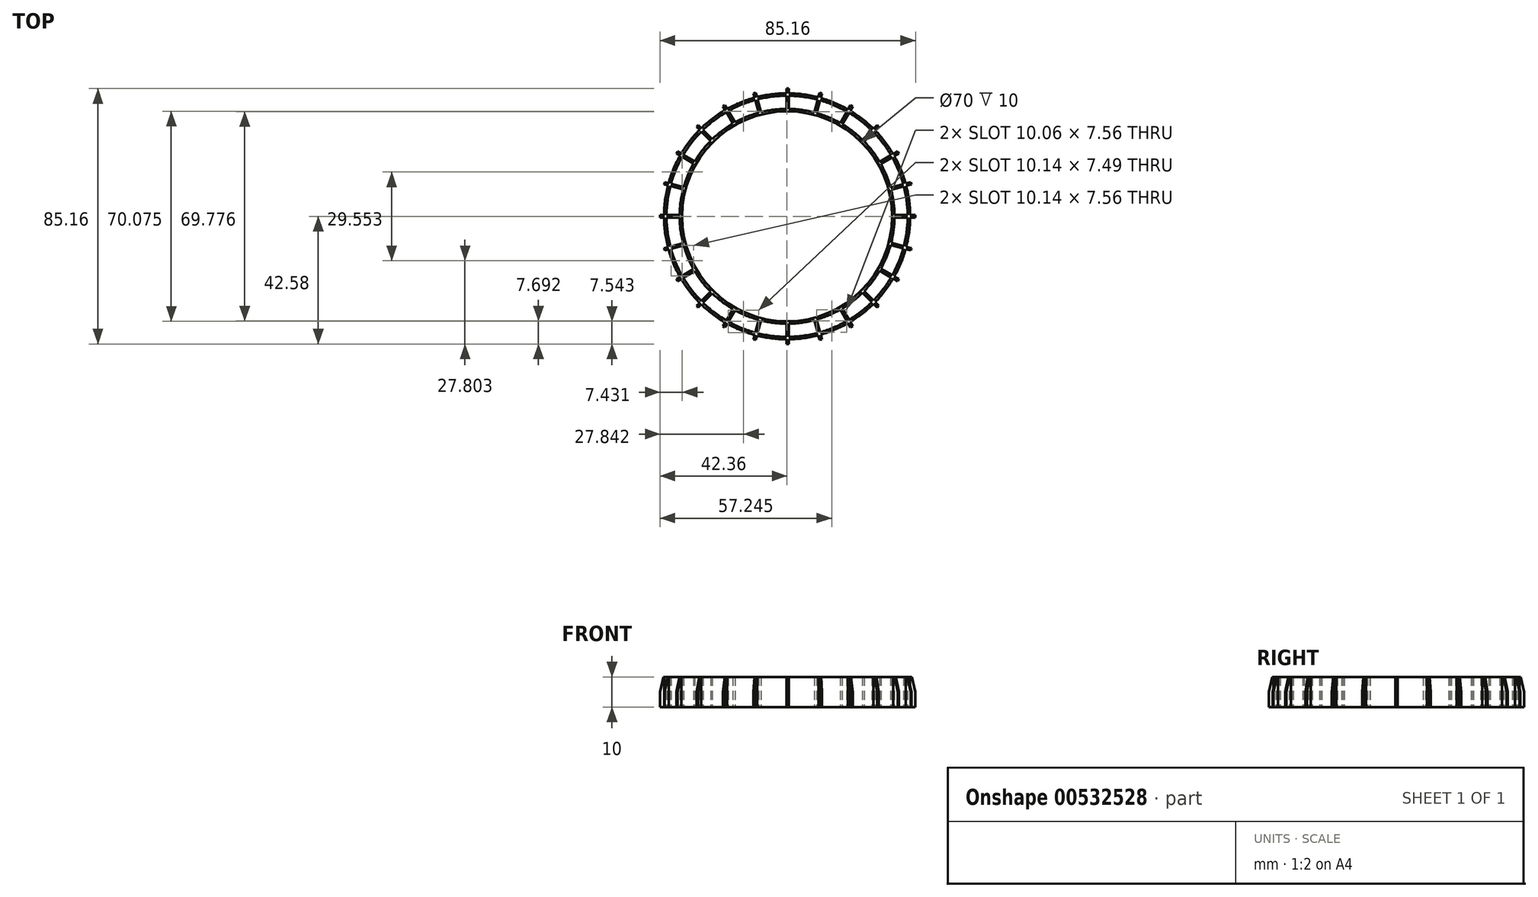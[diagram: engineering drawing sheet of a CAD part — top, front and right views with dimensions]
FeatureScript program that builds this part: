
annotation { "Feature Type Name" : "Feature", "Feature Type Description" : "" }
export const myFeature = defineFeature(function(context is Context, id is Id, definition is map)
    precondition{}
    {
        {
            var Q0;
            Q0=qCreatedBy(makeId("Top.planeOp"),FACE);
            var sketch = newSketch(context, id + "F0", { "sketchPlane" : qUnion([Q0])});
            skCircle(sketch, "E0", {"center": v(0, 0) * mm, "radius": 35 * mm});
            skCircle(sketch, "E1", {"center": v(0, 0) * mm, "radius": 35.8 * mm});
            skCircle(sketch, "E2", {"center": v(0, 0) * mm, "radius": 40.2 * mm});
            skCircle(sketch, "E3", {"center": v(0, 0) * mm, "radius": 41 * mm});
            skLineSegment(sketch, "E4", {"start": v(35.8, 0.4) * mm, "end": v(42.8, 0.4) * mm});
            skLineSegment(sketch, "E5", {"start": v(42.8, 0.4) * mm, "end": v(42.8, 0) * mm});
            skLineSegment(sketch, "E6.MirrorCS", {"start": v(35.8, -0.4) * mm, "end": v(42.8, -0.4) * mm});
            skLineSegment(sketch, "E7.MirrorCS", {"start": v(42.8, -0.4) * mm, "end": v(42.8, 0) * mm});
            skLineSegment(sketch, "E8.1.0", {"start": v(34.48, 9.6) * mm, "end": v(41.24, 11.4) * mm});
            skLineSegment(sketch, "E8.1.1", {"start": v(41.45, 10.63) * mm, "end": v(41.35, 11.02) * mm});
            skLineSegment(sketch, "E8.1.2", {"start": v(41.24, 11.4) * mm, "end": v(41.35, 11.02) * mm});
            skLineSegment(sketch, "E8.1.3", {"start": v(34.69, 8.82) * mm, "end": v(41.45, 10.63) * mm});
            skLineSegment(sketch, "E8.2.0", {"start": v(30.83, 18.14) * mm, "end": v(36.9, 21.64) * mm});
            skLineSegment(sketch, "E8.2.1", {"start": v(37.3, 20.94) * mm, "end": v(37.1, 21.29) * mm});
            skLineSegment(sketch, "E8.2.2", {"start": v(36.9, 21.64) * mm, "end": v(37.1, 21.29) * mm});
            skLineSegment(sketch, "E8.2.3", {"start": v(31.23, 17.44) * mm, "end": v(37.3, 20.94) * mm});
            skLineSegment(sketch, "E8.3.0", {"start": v(25.1, 25.44) * mm, "end": v(30.04, 30.4) * mm});
            skLineSegment(sketch, "E8.3.1", {"start": v(30.6, 29.83) * mm, "end": v(30.33, 30.1) * mm});
            skLineSegment(sketch, "E8.3.2", {"start": v(30.04, 30.4) * mm, "end": v(30.33, 30.1) * mm});
            skLineSegment(sketch, "E8.3.3", {"start": v(25.66, 24.88) * mm, "end": v(30.6, 29.83) * mm});
            skLineSegment(sketch, "E8.4.0", {"start": v(17.66, 31.01) * mm, "end": v(21.16, 37.08) * mm});
            skLineSegment(sketch, "E8.4.1", {"start": v(21.85, 36.68) * mm, "end": v(21.5, 36.88) * mm});
            skLineSegment(sketch, "E8.4.2", {"start": v(21.16, 37.08) * mm, "end": v(21.5, 36.88) * mm});
            skLineSegment(sketch, "E8.4.3", {"start": v(18.35, 30.61) * mm, "end": v(21.85, 36.68) * mm});
            skLineSegment(sketch, "E8.5.0", {"start": v(9.04, 34.47) * mm, "end": v(10.85, 41.23) * mm});
            skLineSegment(sketch, "E8.5.1", {"start": v(11.62, 41.03) * mm, "end": v(11.24, 41.13) * mm});
            skLineSegment(sketch, "E8.5.2", {"start": v(10.85, 41.23) * mm, "end": v(11.24, 41.13) * mm});
            skLineSegment(sketch, "E8.5.3", {"start": v(9.81, 34.26) * mm, "end": v(11.62, 41.03) * mm});
            skLineSegment(sketch, "E8.6.0", {"start": v(-0.18, 35.58) * mm, "end": v(-0.18, 42.58) * mm});
            skLineSegment(sketch, "E8.6.1", {"start": v(0.62, 42.58) * mm, "end": v(0.22, 42.58) * mm});
            skLineSegment(sketch, "E8.6.2", {"start": v(-0.18, 42.58) * mm, "end": v(0.22, 42.58) * mm});
            skLineSegment(sketch, "E8.6.3", {"start": v(0.62, 35.58) * mm, "end": v(0.62, 42.58) * mm});
            skLineSegment(sketch, "E8.7.0", {"start": v(-9.38, 34.26) * mm, "end": v(-11.19, 41.03) * mm});
            skLineSegment(sketch, "E8.7.1", {"start": v(-10.42, 41.23) * mm, "end": v(-10.8, 41.13) * mm});
            skLineSegment(sketch, "E8.7.2", {"start": v(-11.19, 41.03) * mm, "end": v(-10.8, 41.13) * mm});
            skLineSegment(sketch, "E8.7.3", {"start": v(-8.6, 34.47) * mm, "end": v(-10.42, 41.23) * mm});
            skLineSegment(sketch, "E8.8.0", {"start": v(-17.92, 30.61) * mm, "end": v(-21.42, 36.68) * mm});
            skLineSegment(sketch, "E8.8.1", {"start": v(-20.73, 37.08) * mm, "end": v(-21.07, 36.88) * mm});
            skLineSegment(sketch, "E8.8.2", {"start": v(-21.42, 36.68) * mm, "end": v(-21.07, 36.88) * mm});
            skLineSegment(sketch, "E8.8.3", {"start": v(-17.23, 31.01) * mm, "end": v(-20.73, 37.08) * mm});
            skLineSegment(sketch, "E8.9.0", {"start": v(-25.22, 24.88) * mm, "end": v(-30.17, 29.83) * mm});
            skLineSegment(sketch, "E8.9.1", {"start": v(-29.6, 30.4) * mm, "end": v(-29.9, 30.1) * mm});
            skLineSegment(sketch, "E8.9.2", {"start": v(-30.17, 29.83) * mm, "end": v(-29.9, 30.1) * mm});
            skLineSegment(sketch, "E8.9.3", {"start": v(-24.66, 25.44) * mm, "end": v(-29.6, 30.4) * mm});
            skLineSegment(sketch, "E8.10.0", {"start": v(-30.8, 17.44) * mm, "end": v(-36.86, 20.94) * mm});
            skLineSegment(sketch, "E8.10.1", {"start": v(-36.46, 21.64) * mm, "end": v(-36.66, 21.29) * mm});
            skLineSegment(sketch, "E8.10.2", {"start": v(-36.86, 20.94) * mm, "end": v(-36.66, 21.29) * mm});
            skLineSegment(sketch, "E8.10.3", {"start": v(-30.4, 18.14) * mm, "end": v(-36.46, 21.64) * mm});
            skLineSegment(sketch, "E8.11.0", {"start": v(-34.25, 8.82) * mm, "end": v(-41.01, 10.63) * mm});
            skLineSegment(sketch, "E8.11.1", {"start": v(-40.8, 11.4) * mm, "end": v(-40.91, 11.02) * mm});
            skLineSegment(sketch, "E8.11.2", {"start": v(-41.01, 10.63) * mm, "end": v(-40.91, 11.02) * mm});
            skLineSegment(sketch, "E8.11.3", {"start": v(-34.05, 9.6) * mm, "end": v(-40.8, 11.4) * mm});
            skLineSegment(sketch, "E8.12.0", {"start": v(-35.36, -0.4) * mm, "end": v(-42.36, -0.4) * mm});
            skLineSegment(sketch, "E8.12.1", {"start": v(-42.36, 0.4) * mm, "end": v(-42.36, 0) * mm});
            skLineSegment(sketch, "E8.12.2", {"start": v(-42.36, -0.4) * mm, "end": v(-42.36, 0) * mm});
            skLineSegment(sketch, "E8.12.3", {"start": v(-35.36, 0.4) * mm, "end": v(-42.36, 0.4) * mm});
            skLineSegment(sketch, "E8.13.0", {"start": v(-34.05, -9.6) * mm, "end": v(-40.8, -11.4) * mm});
            skLineSegment(sketch, "E8.13.1", {"start": v(-41.01, -10.63) * mm, "end": v(-40.91, -11.02) * mm});
            skLineSegment(sketch, "E8.13.2", {"start": v(-40.8, -11.4) * mm, "end": v(-40.91, -11.02) * mm});
            skLineSegment(sketch, "E8.13.3", {"start": v(-34.25, -8.82) * mm, "end": v(-41.01, -10.63) * mm});
            skLineSegment(sketch, "E8.14.0", {"start": v(-30.4, -18.14) * mm, "end": v(-36.46, -21.64) * mm});
            skLineSegment(sketch, "E8.14.1", {"start": v(-36.86, -20.94) * mm, "end": v(-36.66, -21.29) * mm});
            skLineSegment(sketch, "E8.14.2", {"start": v(-36.46, -21.64) * mm, "end": v(-36.66, -21.29) * mm});
            skLineSegment(sketch, "E8.14.3", {"start": v(-30.8, -17.44) * mm, "end": v(-36.86, -20.94) * mm});
            skLineSegment(sketch, "E8.15.0", {"start": v(-24.66, -25.44) * mm, "end": v(-29.6, -30.4) * mm});
            skLineSegment(sketch, "E8.15.1", {"start": v(-30.17, -29.83) * mm, "end": v(-29.9, -30.1) * mm});
            skLineSegment(sketch, "E8.15.2", {"start": v(-29.6, -30.4) * mm, "end": v(-29.9, -30.1) * mm});
            skLineSegment(sketch, "E8.15.3", {"start": v(-25.22, -24.88) * mm, "end": v(-30.17, -29.83) * mm});
            skLineSegment(sketch, "E8.16.0", {"start": v(-17.23, -31.01) * mm, "end": v(-20.73, -37.08) * mm});
            skLineSegment(sketch, "E8.16.1", {"start": v(-21.42, -36.68) * mm, "end": v(-21.07, -36.88) * mm});
            skLineSegment(sketch, "E8.16.2", {"start": v(-20.73, -37.08) * mm, "end": v(-21.07, -36.88) * mm});
            skLineSegment(sketch, "E8.16.3", {"start": v(-17.92, -30.61) * mm, "end": v(-21.42, -36.68) * mm});
            skLineSegment(sketch, "E8.17.0", {"start": v(-8.6, -34.47) * mm, "end": v(-10.42, -41.23) * mm});
            skLineSegment(sketch, "E8.17.1", {"start": v(-11.19, -41.03) * mm, "end": v(-10.8, -41.13) * mm});
            skLineSegment(sketch, "E8.17.2", {"start": v(-10.42, -41.23) * mm, "end": v(-10.8, -41.13) * mm});
            skLineSegment(sketch, "E8.17.3", {"start": v(-9.38, -34.26) * mm, "end": v(-11.19, -41.03) * mm});
            skLineSegment(sketch, "E8.18.0", {"start": v(0.62, -35.58) * mm, "end": v(0.62, -42.58) * mm});
            skLineSegment(sketch, "E8.18.1", {"start": v(-0.18, -42.58) * mm, "end": v(0.22, -42.58) * mm});
            skLineSegment(sketch, "E8.18.2", {"start": v(0.62, -42.58) * mm, "end": v(0.22, -42.58) * mm});
            skLineSegment(sketch, "E8.18.3", {"start": v(-0.18, -35.58) * mm, "end": v(-0.18, -42.58) * mm});
            skLineSegment(sketch, "E8.19.0", {"start": v(9.81, -34.26) * mm, "end": v(11.62, -41.03) * mm});
            skLineSegment(sketch, "E8.19.1", {"start": v(10.85, -41.23) * mm, "end": v(11.24, -41.13) * mm});
            skLineSegment(sketch, "E8.19.2", {"start": v(11.62, -41.03) * mm, "end": v(11.24, -41.13) * mm});
            skLineSegment(sketch, "E8.19.3", {"start": v(9.04, -34.47) * mm, "end": v(10.85, -41.23) * mm});
            skLineSegment(sketch, "E8.20.0", {"start": v(18.35, -30.61) * mm, "end": v(21.85, -36.68) * mm});
            skLineSegment(sketch, "E8.20.1", {"start": v(21.16, -37.08) * mm, "end": v(21.5, -36.88) * mm});
            skLineSegment(sketch, "E8.20.2", {"start": v(21.85, -36.68) * mm, "end": v(21.5, -36.88) * mm});
            skLineSegment(sketch, "E8.20.3", {"start": v(17.66, -31.01) * mm, "end": v(21.16, -37.08) * mm});
            skLineSegment(sketch, "E8.21.0", {"start": v(25.66, -24.88) * mm, "end": v(30.6, -29.83) * mm});
            skLineSegment(sketch, "E8.21.1", {"start": v(30.04, -30.4) * mm, "end": v(30.33, -30.1) * mm});
            skLineSegment(sketch, "E8.21.2", {"start": v(30.6, -29.83) * mm, "end": v(30.33, -30.1) * mm});
            skLineSegment(sketch, "E8.21.3", {"start": v(25.1, -25.44) * mm, "end": v(30.04, -30.4) * mm});
            skLineSegment(sketch, "E8.22.0", {"start": v(31.23, -17.44) * mm, "end": v(37.3, -20.94) * mm});
            skLineSegment(sketch, "E8.22.1", {"start": v(36.9, -21.64) * mm, "end": v(37.1, -21.29) * mm});
            skLineSegment(sketch, "E8.22.2", {"start": v(37.3, -20.94) * mm, "end": v(37.1, -21.29) * mm});
            skLineSegment(sketch, "E8.22.3", {"start": v(30.83, -18.14) * mm, "end": v(36.9, -21.64) * mm});
            skLineSegment(sketch, "E8.23.0", {"start": v(34.69, -8.82) * mm, "end": v(41.45, -10.63) * mm});
            skLineSegment(sketch, "E8.23.1", {"start": v(41.24, -11.4) * mm, "end": v(41.35, -11.02) * mm});
            skLineSegment(sketch, "E8.23.2", {"start": v(41.45, -10.63) * mm, "end": v(41.35, -11.02) * mm});
            skLineSegment(sketch, "E8.23.3", {"start": v(34.48, -9.6) * mm, "end": v(41.24, -11.4) * mm});
            skPoint(sketch, "E8.center", {"position": v(0.22, 0) * mm});
            skSolve(sketch);
        }
        {
            var Q0;
            {var subQ1=sQuery(id+"F0.wireOp",EDGE,"E8.1.1");Q0=makeQuery(id+"F0.imprint","IMPRINT",FACE,{"disambiguationData":[TD([[makeQuery(id+"F0.imprint","IMPRINT",EDGE,{"derivedFrom":subQ1}),1.0]])]});}
            var Q1;
            {var subQ0=sQuery(id+"F0.wireOp",EDGE,"E8.2.1");Q1=makeQuery(id+"F0.imprint","IMPRINT",FACE,{"disambiguationData":[TD([[makeQuery(id+"F0.imprint","IMPRINT",EDGE,{"derivedFrom":subQ0}),1.0]])]});}
            var Q2;
            {var subQ4=sQuery(id+"F0.wireOp",EDGE,"E8.3.1");Q2=makeQuery(id+"F0.imprint","IMPRINT",FACE,{"disambiguationData":[TD([[makeQuery(id+"F0.imprint","IMPRINT",EDGE,{"derivedFrom":subQ4}),1.0]])]});}
            var Q3;
            {var subQ6=sQuery(id+"F0.wireOp",EDGE,"E8.4.1");Q3=makeQuery(id+"F0.imprint","IMPRINT",FACE,{"disambiguationData":[TD([[makeQuery(id+"F0.imprint","IMPRINT",EDGE,{"derivedFrom":subQ6}),1.0]])]});}
            var Q4;
            {var subQ1=sQuery(id+"F0.wireOp",EDGE,"E8.5.1");Q4=makeQuery(id+"F0.imprint","IMPRINT",FACE,{"disambiguationData":[TD([[makeQuery(id+"F0.imprint","IMPRINT",EDGE,{"derivedFrom":subQ1}),1.0]])]});}
            var Q5;
            {var subQ1=sQuery(id+"F0.wireOp",EDGE,"E8.6.1");Q5=makeQuery(id+"F0.imprint","IMPRINT",FACE,{"disambiguationData":[TD([[makeQuery(id+"F0.imprint","IMPRINT",EDGE,{"derivedFrom":subQ1}),1.0]])]});}
            var Q6;
            {var subQ0=sQuery(id+"F0.wireOp",EDGE,"E8.7.1");Q6=makeQuery(id+"F0.imprint","IMPRINT",FACE,{"disambiguationData":[TD([[makeQuery(id+"F0.imprint","IMPRINT",EDGE,{"derivedFrom":subQ0}),1.0]])]});}
            var Q7;
            {var subQ6=sQuery(id+"F0.wireOp",EDGE,"E8.8.1");Q7=makeQuery(id+"F0.imprint","IMPRINT",FACE,{"disambiguationData":[TD([[makeQuery(id+"F0.imprint","IMPRINT",EDGE,{"derivedFrom":subQ6}),1.0]])]});}
            var Q8;
            {var subQ1=sQuery(id+"F0.wireOp",EDGE,"E8.9.1");Q8=makeQuery(id+"F0.imprint","IMPRINT",FACE,{"disambiguationData":[TD([[makeQuery(id+"F0.imprint","IMPRINT",EDGE,{"derivedFrom":subQ1}),1.0]])]});}
            var Q9;
            {var subQ1=sQuery(id+"F0.wireOp",EDGE,"E8.10.1");Q9=makeQuery(id+"F0.imprint","IMPRINT",FACE,{"disambiguationData":[TD([[makeQuery(id+"F0.imprint","IMPRINT",EDGE,{"derivedFrom":subQ1}),1.0]])]});}
            var Q10;
            {var subQ1=sQuery(id+"F0.wireOp",EDGE,"E8.11.1");Q10=makeQuery(id+"F0.imprint","IMPRINT",FACE,{"disambiguationData":[TD([[makeQuery(id+"F0.imprint","IMPRINT",EDGE,{"derivedFrom":subQ1}),1.0]])]});}
            var Q11;
            {var subQ0=sQuery(id+"F0.wireOp",EDGE,"E8.12.1");Q11=makeQuery(id+"F0.imprint","IMPRINT",FACE,{"disambiguationData":[TD([[makeQuery(id+"F0.imprint","IMPRINT",EDGE,{"derivedFrom":subQ0}),1.0]])]});}
            var Q12;
            {var subQ4=sQuery(id+"F0.wireOp",EDGE,"E8.13.1");Q12=makeQuery(id+"F0.imprint","IMPRINT",FACE,{"disambiguationData":[TD([[makeQuery(id+"F0.imprint","IMPRINT",EDGE,{"derivedFrom":subQ4}),1.0]])]});}
            var Q13;
            {var subQ1=sQuery(id+"F0.wireOp",EDGE,"E8.14.1");Q13=makeQuery(id+"F0.imprint","IMPRINT",FACE,{"disambiguationData":[TD([[makeQuery(id+"F0.imprint","IMPRINT",EDGE,{"derivedFrom":subQ1}),1.0]])]});}
            var Q14;
            {var subQ6=sQuery(id+"F0.wireOp",EDGE,"E8.15.1");Q14=makeQuery(id+"F0.imprint","IMPRINT",FACE,{"disambiguationData":[TD([[makeQuery(id+"F0.imprint","IMPRINT",EDGE,{"derivedFrom":subQ6}),1.0]])]});}
            var Q15;
            {var subQ1=sQuery(id+"F0.wireOp",EDGE,"E8.16.1");Q15=makeQuery(id+"F0.imprint","IMPRINT",FACE,{"disambiguationData":[TD([[makeQuery(id+"F0.imprint","IMPRINT",EDGE,{"derivedFrom":subQ1}),1.0]])]});}
            var Q16;
            {var subQ0=sQuery(id+"F0.wireOp",EDGE,"E8.17.1");Q16=makeQuery(id+"F0.imprint","IMPRINT",FACE,{"disambiguationData":[TD([[makeQuery(id+"F0.imprint","IMPRINT",EDGE,{"derivedFrom":subQ0}),1.0]])]});}
            var Q17;
            {var subQ4=sQuery(id+"F0.wireOp",EDGE,"E8.18.1");Q17=makeQuery(id+"F0.imprint","IMPRINT",FACE,{"disambiguationData":[TD([[makeQuery(id+"F0.imprint","IMPRINT",EDGE,{"derivedFrom":subQ4}),1.0]])]});}
            var Q18;
            {var subQ1=sQuery(id+"F0.wireOp",EDGE,"E8.19.1");Q18=makeQuery(id+"F0.imprint","IMPRINT",FACE,{"disambiguationData":[TD([[makeQuery(id+"F0.imprint","IMPRINT",EDGE,{"derivedFrom":subQ1}),1.0]])]});}
            var Q19;
            {var subQ1=sQuery(id+"F0.wireOp",EDGE,"E8.20.1");Q19=makeQuery(id+"F0.imprint","IMPRINT",FACE,{"disambiguationData":[TD([[makeQuery(id+"F0.imprint","IMPRINT",EDGE,{"derivedFrom":subQ1}),1.0]])]});}
            var Q20;
            {var subQ1=sQuery(id+"F0.wireOp",EDGE,"E8.21.1");Q20=makeQuery(id+"F0.imprint","IMPRINT",FACE,{"disambiguationData":[TD([[makeQuery(id+"F0.imprint","IMPRINT",EDGE,{"derivedFrom":subQ1}),1.0]])]});}
            var Q21;
            {var subQ0=sQuery(id+"F0.wireOp",EDGE,"E8.22.1");Q21=makeQuery(id+"F0.imprint","IMPRINT",FACE,{"disambiguationData":[TD([[makeQuery(id+"F0.imprint","IMPRINT",EDGE,{"derivedFrom":subQ0}),1.0]])]});}
            var Q22;
            {var subQ4=sQuery(id+"F0.wireOp",EDGE,"E8.23.1");Q22=makeQuery(id+"F0.imprint","IMPRINT",FACE,{"disambiguationData":[TD([[makeQuery(id+"F0.imprint","IMPRINT",EDGE,{"derivedFrom":subQ4}),1.0]])]});}
            var Q23;
            {var subQ4=sQuery(id+"F0.wireOp",EDGE,"E5");Q23=makeQuery(id+"F0.imprint","IMPRINT",FACE,{"disambiguationData":[TD([[makeQuery(id+"F0.imprint","IMPRINT",EDGE,{"derivedFrom":subQ4}),-1.0]])]});}
            var Q24;
            {var subQ0=sQuery(id+"F0.wireOp",EDGE,"E8.1.3");var subQ1=sQuery(id+"F0.wireOp",EDGE,"E2");var subQ2=makeQuery(id+"F0.imprint","INTERSECT",VERTEX,{"derivedFrom":[subQ1,subQ0]});Q24=makeQuery(id+"F0.imprint","IMPRINT",FACE,{"disambiguationData":[TD([[makeQuery(id+"F0.imprint","IMPRINT",EDGE,{"disambiguationData":[TD([[subQ2,1.0]])],"derivedFrom":subQ1}),-1.0]])]});}
            var Q25;
            {var subQ0=sQuery(id+"F0.wireOp",EDGE,"E8.1.0");var subQ1=sQuery(id+"F0.wireOp",EDGE,"E2");var subQ2=makeQuery(id+"F0.imprint","INTERSECT",VERTEX,{"derivedFrom":[subQ1,subQ0]});Q25=makeQuery(id+"F0.imprint","IMPRINT",FACE,{"disambiguationData":[TD([[makeQuery(id+"F0.imprint","IMPRINT",EDGE,{"disambiguationData":[TD([[subQ2,-1.0]])],"derivedFrom":subQ1}),-1.0]])]});}
            var Q26;
            {var subQ0=sQuery(id+"F0.wireOp",EDGE,"E8.2.0");var subQ1=sQuery(id+"F0.wireOp",EDGE,"E2");var subQ2=makeQuery(id+"F0.imprint","INTERSECT",VERTEX,{"derivedFrom":[subQ1,subQ0]});Q26=makeQuery(id+"F0.imprint","IMPRINT",FACE,{"disambiguationData":[TD([[makeQuery(id+"F0.imprint","IMPRINT",EDGE,{"disambiguationData":[TD([[subQ2,-1.0]])],"derivedFrom":subQ1}),-1.0]])]});}
            var Q27;
            {var subQ0=sQuery(id+"F0.wireOp",EDGE,"E8.3.0");var subQ1=sQuery(id+"F0.wireOp",EDGE,"E2");var subQ2=makeQuery(id+"F0.imprint","INTERSECT",VERTEX,{"derivedFrom":[subQ1,subQ0]});Q27=makeQuery(id+"F0.imprint","IMPRINT",FACE,{"disambiguationData":[TD([[makeQuery(id+"F0.imprint","IMPRINT",EDGE,{"disambiguationData":[TD([[subQ2,-1.0]])],"derivedFrom":subQ1}),-1.0]])]});}
            var Q28;
            {var subQ0=sQuery(id+"F0.wireOp",EDGE,"E8.4.0");var subQ1=sQuery(id+"F0.wireOp",EDGE,"E2");var subQ2=makeQuery(id+"F0.imprint","INTERSECT",VERTEX,{"derivedFrom":[subQ1,subQ0]});Q28=makeQuery(id+"F0.imprint","IMPRINT",FACE,{"disambiguationData":[TD([[makeQuery(id+"F0.imprint","IMPRINT",EDGE,{"disambiguationData":[TD([[subQ2,-1.0]])],"derivedFrom":subQ1}),-1.0]])]});}
            var Q29;
            {var subQ0=sQuery(id+"F0.wireOp",EDGE,"E8.5.0");var subQ1=sQuery(id+"F0.wireOp",EDGE,"E2");var subQ2=makeQuery(id+"F0.imprint","INTERSECT",VERTEX,{"derivedFrom":[subQ1,subQ0]});Q29=makeQuery(id+"F0.imprint","IMPRINT",FACE,{"disambiguationData":[TD([[makeQuery(id+"F0.imprint","IMPRINT",EDGE,{"disambiguationData":[TD([[subQ2,-1.0]])],"derivedFrom":subQ1}),-1.0]])]});}
            var Q30;
            {var subQ0=sQuery(id+"F0.wireOp",EDGE,"E8.6.0");var subQ1=sQuery(id+"F0.wireOp",EDGE,"E2");var subQ2=makeQuery(id+"F0.imprint","INTERSECT",VERTEX,{"derivedFrom":[subQ1,subQ0]});Q30=makeQuery(id+"F0.imprint","IMPRINT",FACE,{"disambiguationData":[TD([[makeQuery(id+"F0.imprint","IMPRINT",EDGE,{"disambiguationData":[TD([[subQ2,-1.0]])],"derivedFrom":subQ1}),-1.0]])]});}
            var Q31;
            {var subQ0=sQuery(id+"F0.wireOp",EDGE,"E8.7.0");var subQ1=sQuery(id+"F0.wireOp",EDGE,"E2");var subQ2=makeQuery(id+"F0.imprint","INTERSECT",VERTEX,{"derivedFrom":[subQ1,subQ0]});Q31=makeQuery(id+"F0.imprint","IMPRINT",FACE,{"disambiguationData":[TD([[makeQuery(id+"F0.imprint","IMPRINT",EDGE,{"disambiguationData":[TD([[subQ2,-1.0]])],"derivedFrom":subQ1}),-1.0]])]});}
            var Q32;
            {var subQ0=sQuery(id+"F0.wireOp",EDGE,"E8.8.0");var subQ1=sQuery(id+"F0.wireOp",EDGE,"E2");var subQ2=makeQuery(id+"F0.imprint","INTERSECT",VERTEX,{"derivedFrom":[subQ1,subQ0]});Q32=makeQuery(id+"F0.imprint","IMPRINT",FACE,{"disambiguationData":[TD([[makeQuery(id+"F0.imprint","IMPRINT",EDGE,{"disambiguationData":[TD([[subQ2,-1.0]])],"derivedFrom":subQ1}),-1.0]])]});}
            var Q33;
            {var subQ0=sQuery(id+"F0.wireOp",EDGE,"E8.9.0");var subQ1=sQuery(id+"F0.wireOp",EDGE,"E2");var subQ2=makeQuery(id+"F0.imprint","INTERSECT",VERTEX,{"derivedFrom":[subQ1,subQ0]});Q33=makeQuery(id+"F0.imprint","IMPRINT",FACE,{"disambiguationData":[TD([[makeQuery(id+"F0.imprint","IMPRINT",EDGE,{"disambiguationData":[TD([[subQ2,-1.0]])],"derivedFrom":subQ1}),-1.0]])]});}
            var Q34;
            {var subQ0=sQuery(id+"F0.wireOp",EDGE,"E8.10.0");var subQ1=sQuery(id+"F0.wireOp",EDGE,"E2");var subQ2=makeQuery(id+"F0.imprint","INTERSECT",VERTEX,{"derivedFrom":[subQ1,subQ0]});Q34=makeQuery(id+"F0.imprint","IMPRINT",FACE,{"disambiguationData":[TD([[makeQuery(id+"F0.imprint","IMPRINT",EDGE,{"disambiguationData":[TD([[subQ2,-1.0]])],"derivedFrom":subQ1}),-1.0]])]});}
            var Q35;
            {var subQ0=sQuery(id+"F0.wireOp",EDGE,"E8.11.0");var subQ1=sQuery(id+"F0.wireOp",EDGE,"E2");var subQ2=makeQuery(id+"F0.imprint","INTERSECT",VERTEX,{"derivedFrom":[subQ1,subQ0]});Q35=makeQuery(id+"F0.imprint","IMPRINT",FACE,{"disambiguationData":[TD([[makeQuery(id+"F0.imprint","IMPRINT",EDGE,{"disambiguationData":[TD([[subQ2,-1.0]])],"derivedFrom":subQ1}),-1.0]])]});}
            var Q36;
            {var subQ0=sQuery(id+"F0.wireOp",EDGE,"E8.12.0");var subQ1=sQuery(id+"F0.wireOp",EDGE,"E2");var subQ2=makeQuery(id+"F0.imprint","INTERSECT",VERTEX,{"derivedFrom":[subQ1,subQ0]});Q36=makeQuery(id+"F0.imprint","IMPRINT",FACE,{"disambiguationData":[TD([[makeQuery(id+"F0.imprint","IMPRINT",EDGE,{"disambiguationData":[TD([[subQ2,-1.0]])],"derivedFrom":subQ1}),-1.0]])]});}
            var Q37;
            {var subQ0=sQuery(id+"F0.wireOp",EDGE,"E8.13.0");var subQ1=sQuery(id+"F0.wireOp",EDGE,"E2");var subQ2=makeQuery(id+"F0.imprint","INTERSECT",VERTEX,{"derivedFrom":[subQ1,subQ0]});Q37=makeQuery(id+"F0.imprint","IMPRINT",FACE,{"disambiguationData":[TD([[makeQuery(id+"F0.imprint","IMPRINT",EDGE,{"disambiguationData":[TD([[subQ2,-1.0]])],"derivedFrom":subQ1}),-1.0]])]});}
            var Q38;
            {var subQ0=sQuery(id+"F0.wireOp",EDGE,"E8.14.0");var subQ1=sQuery(id+"F0.wireOp",EDGE,"E2");var subQ2=makeQuery(id+"F0.imprint","INTERSECT",VERTEX,{"derivedFrom":[subQ1,subQ0]});Q38=makeQuery(id+"F0.imprint","IMPRINT",FACE,{"disambiguationData":[TD([[makeQuery(id+"F0.imprint","IMPRINT",EDGE,{"disambiguationData":[TD([[subQ2,-1.0]])],"derivedFrom":subQ1}),-1.0]])]});}
            var Q39;
            {var subQ0=sQuery(id+"F0.wireOp",EDGE,"E8.15.0");var subQ1=sQuery(id+"F0.wireOp",EDGE,"E2");var subQ2=makeQuery(id+"F0.imprint","INTERSECT",VERTEX,{"derivedFrom":[subQ1,subQ0]});Q39=makeQuery(id+"F0.imprint","IMPRINT",FACE,{"disambiguationData":[TD([[makeQuery(id+"F0.imprint","IMPRINT",EDGE,{"disambiguationData":[TD([[subQ2,-1.0]])],"derivedFrom":subQ1}),-1.0]])]});}
            var Q40;
            {var subQ0=sQuery(id+"F0.wireOp",EDGE,"E8.16.0");var subQ1=sQuery(id+"F0.wireOp",EDGE,"E2");var subQ2=makeQuery(id+"F0.imprint","INTERSECT",VERTEX,{"derivedFrom":[subQ1,subQ0]});Q40=makeQuery(id+"F0.imprint","IMPRINT",FACE,{"disambiguationData":[TD([[makeQuery(id+"F0.imprint","IMPRINT",EDGE,{"disambiguationData":[TD([[subQ2,-1.0]])],"derivedFrom":subQ1}),-1.0]])]});}
            var Q41;
            {var subQ0=sQuery(id+"F0.wireOp",EDGE,"E8.17.0");var subQ1=sQuery(id+"F0.wireOp",EDGE,"E2");var subQ2=makeQuery(id+"F0.imprint","INTERSECT",VERTEX,{"derivedFrom":[subQ1,subQ0]});Q41=makeQuery(id+"F0.imprint","IMPRINT",FACE,{"disambiguationData":[TD([[makeQuery(id+"F0.imprint","IMPRINT",EDGE,{"disambiguationData":[TD([[subQ2,-1.0]])],"derivedFrom":subQ1}),-1.0]])]});}
            var Q42;
            {var subQ0=sQuery(id+"F0.wireOp",EDGE,"E8.18.0");var subQ1=sQuery(id+"F0.wireOp",EDGE,"E2");var subQ2=makeQuery(id+"F0.imprint","INTERSECT",VERTEX,{"derivedFrom":[subQ1,subQ0]});Q42=makeQuery(id+"F0.imprint","IMPRINT",FACE,{"disambiguationData":[TD([[makeQuery(id+"F0.imprint","IMPRINT",EDGE,{"disambiguationData":[TD([[subQ2,-1.0]])],"derivedFrom":subQ1}),-1.0]])]});}
            var Q43;
            {var subQ0=sQuery(id+"F0.wireOp",EDGE,"E8.19.0");var subQ1=sQuery(id+"F0.wireOp",EDGE,"E2");var subQ2=makeQuery(id+"F0.imprint","INTERSECT",VERTEX,{"derivedFrom":[subQ1,subQ0]});Q43=makeQuery(id+"F0.imprint","IMPRINT",FACE,{"disambiguationData":[TD([[makeQuery(id+"F0.imprint","IMPRINT",EDGE,{"disambiguationData":[TD([[subQ2,-1.0]])],"derivedFrom":subQ1}),-1.0]])]});}
            var Q44;
            {var subQ0=sQuery(id+"F0.wireOp",EDGE,"E8.20.0");var subQ1=sQuery(id+"F0.wireOp",EDGE,"E2");var subQ2=makeQuery(id+"F0.imprint","INTERSECT",VERTEX,{"derivedFrom":[subQ1,subQ0]});Q44=makeQuery(id+"F0.imprint","IMPRINT",FACE,{"disambiguationData":[TD([[makeQuery(id+"F0.imprint","IMPRINT",EDGE,{"disambiguationData":[TD([[subQ2,-1.0]])],"derivedFrom":subQ1}),-1.0]])]});}
            var Q45;
            {var subQ0=sQuery(id+"F0.wireOp",EDGE,"E8.21.0");var subQ1=sQuery(id+"F0.wireOp",EDGE,"E2");var subQ2=makeQuery(id+"F0.imprint","INTERSECT",VERTEX,{"derivedFrom":[subQ1,subQ0]});Q45=makeQuery(id+"F0.imprint","IMPRINT",FACE,{"disambiguationData":[TD([[makeQuery(id+"F0.imprint","IMPRINT",EDGE,{"disambiguationData":[TD([[subQ2,-1.0]])],"derivedFrom":subQ1}),-1.0]])]});}
            var Q46;
            {var subQ0=sQuery(id+"F0.wireOp",EDGE,"E8.22.0");var subQ1=sQuery(id+"F0.wireOp",EDGE,"E2");var subQ2=makeQuery(id+"F0.imprint","INTERSECT",VERTEX,{"derivedFrom":[subQ1,subQ0]});Q46=makeQuery(id+"F0.imprint","IMPRINT",FACE,{"disambiguationData":[TD([[makeQuery(id+"F0.imprint","IMPRINT",EDGE,{"disambiguationData":[TD([[subQ2,-1.0]])],"derivedFrom":subQ1}),-1.0]])]});}
            var Q47;
            {var subQ0=sQuery(id+"F0.wireOp",EDGE,"E8.23.0");var subQ1=sQuery(id+"F0.wireOp",EDGE,"E2");var subQ2=makeQuery(id+"F0.imprint","INTERSECT",VERTEX,{"derivedFrom":[subQ1,subQ0]});Q47=makeQuery(id+"F0.imprint","IMPRINT",FACE,{"disambiguationData":[TD([[makeQuery(id+"F0.imprint","IMPRINT",EDGE,{"disambiguationData":[TD([[subQ2,-1.0]])],"derivedFrom":subQ1}),-1.0]])]});}
            var Q48;
            {var subQ0=sQuery(id+"F0.wireOp",EDGE,"E8.1.3");var subQ1=sQuery(id+"F0.wireOp",EDGE,"E2");var subQ2=makeQuery(id+"F0.imprint","INTERSECT",VERTEX,{"derivedFrom":[subQ1,subQ0]});Q48=makeQuery(id+"F0.imprint","IMPRINT",FACE,{"disambiguationData":[TD([[makeQuery(id+"F0.imprint","IMPRINT",EDGE,{"disambiguationData":[TD([[subQ2,-1.0]])],"derivedFrom":subQ1}),-1.0]])]});}
            var Q49;
            {var subQ0=sQuery(id+"F0.wireOp",EDGE,"E8.2.3");var subQ1=sQuery(id+"F0.wireOp",EDGE,"E2");var subQ2=makeQuery(id+"F0.imprint","INTERSECT",VERTEX,{"derivedFrom":[subQ1,subQ0]});Q49=makeQuery(id+"F0.imprint","IMPRINT",FACE,{"disambiguationData":[TD([[makeQuery(id+"F0.imprint","IMPRINT",EDGE,{"disambiguationData":[TD([[subQ2,-1.0]])],"derivedFrom":subQ1}),-1.0]])]});}
            var Q50;
            {var subQ0=sQuery(id+"F0.wireOp",EDGE,"E8.3.3");var subQ1=sQuery(id+"F0.wireOp",EDGE,"E2");var subQ2=makeQuery(id+"F0.imprint","INTERSECT",VERTEX,{"derivedFrom":[subQ1,subQ0]});Q50=makeQuery(id+"F0.imprint","IMPRINT",FACE,{"disambiguationData":[TD([[makeQuery(id+"F0.imprint","IMPRINT",EDGE,{"disambiguationData":[TD([[subQ2,-1.0]])],"derivedFrom":subQ1}),-1.0]])]});}
            var Q51;
            {var subQ0=sQuery(id+"F0.wireOp",EDGE,"E8.4.3");var subQ1=sQuery(id+"F0.wireOp",EDGE,"E2");var subQ2=makeQuery(id+"F0.imprint","INTERSECT",VERTEX,{"derivedFrom":[subQ1,subQ0]});Q51=makeQuery(id+"F0.imprint","IMPRINT",FACE,{"disambiguationData":[TD([[makeQuery(id+"F0.imprint","IMPRINT",EDGE,{"disambiguationData":[TD([[subQ2,-1.0]])],"derivedFrom":subQ1}),-1.0]])]});}
            var Q52;
            {var subQ0=sQuery(id+"F0.wireOp",EDGE,"E8.5.3");var subQ1=sQuery(id+"F0.wireOp",EDGE,"E2");var subQ2=makeQuery(id+"F0.imprint","INTERSECT",VERTEX,{"derivedFrom":[subQ1,subQ0]});Q52=makeQuery(id+"F0.imprint","IMPRINT",FACE,{"disambiguationData":[TD([[makeQuery(id+"F0.imprint","IMPRINT",EDGE,{"disambiguationData":[TD([[subQ2,-1.0]])],"derivedFrom":subQ1}),-1.0]])]});}
            var Q53;
            {var subQ0=sQuery(id+"F0.wireOp",EDGE,"E8.6.3");var subQ1=sQuery(id+"F0.wireOp",EDGE,"E2");var subQ2=makeQuery(id+"F0.imprint","INTERSECT",VERTEX,{"derivedFrom":[subQ1,subQ0]});Q53=makeQuery(id+"F0.imprint","IMPRINT",FACE,{"disambiguationData":[TD([[makeQuery(id+"F0.imprint","IMPRINT",EDGE,{"disambiguationData":[TD([[subQ2,-1.0]])],"derivedFrom":subQ1}),-1.0]])]});}
            var Q54;
            {var subQ0=sQuery(id+"F0.wireOp",EDGE,"E8.7.3");var subQ1=sQuery(id+"F0.wireOp",EDGE,"E2");var subQ2=makeQuery(id+"F0.imprint","INTERSECT",VERTEX,{"derivedFrom":[subQ1,subQ0]});Q54=makeQuery(id+"F0.imprint","IMPRINT",FACE,{"disambiguationData":[TD([[makeQuery(id+"F0.imprint","IMPRINT",EDGE,{"disambiguationData":[TD([[subQ2,-1.0]])],"derivedFrom":subQ1}),-1.0]])]});}
            var Q55;
            {var subQ0=sQuery(id+"F0.wireOp",EDGE,"E8.8.3");var subQ1=sQuery(id+"F0.wireOp",EDGE,"E2");var subQ2=makeQuery(id+"F0.imprint","INTERSECT",VERTEX,{"derivedFrom":[subQ1,subQ0]});Q55=makeQuery(id+"F0.imprint","IMPRINT",FACE,{"disambiguationData":[TD([[makeQuery(id+"F0.imprint","IMPRINT",EDGE,{"disambiguationData":[TD([[subQ2,-1.0]])],"derivedFrom":subQ1}),-1.0]])]});}
            var Q56;
            {var subQ0=sQuery(id+"F0.wireOp",EDGE,"E8.9.3");var subQ1=sQuery(id+"F0.wireOp",EDGE,"E2");var subQ2=makeQuery(id+"F0.imprint","INTERSECT",VERTEX,{"derivedFrom":[subQ1,subQ0]});Q56=makeQuery(id+"F0.imprint","IMPRINT",FACE,{"disambiguationData":[TD([[makeQuery(id+"F0.imprint","IMPRINT",EDGE,{"disambiguationData":[TD([[subQ2,-1.0]])],"derivedFrom":subQ1}),-1.0]])]});}
            var Q57;
            {var subQ0=sQuery(id+"F0.wireOp",EDGE,"E8.10.3");var subQ1=sQuery(id+"F0.wireOp",EDGE,"E2");var subQ2=makeQuery(id+"F0.imprint","INTERSECT",VERTEX,{"derivedFrom":[subQ1,subQ0]});Q57=makeQuery(id+"F0.imprint","IMPRINT",FACE,{"disambiguationData":[TD([[makeQuery(id+"F0.imprint","IMPRINT",EDGE,{"disambiguationData":[TD([[subQ2,-1.0]])],"derivedFrom":subQ1}),-1.0]])]});}
            var Q58;
            {var subQ0=sQuery(id+"F0.wireOp",EDGE,"E8.11.3");var subQ1=sQuery(id+"F0.wireOp",EDGE,"E2");var subQ2=makeQuery(id+"F0.imprint","INTERSECT",VERTEX,{"derivedFrom":[subQ1,subQ0]});Q58=makeQuery(id+"F0.imprint","IMPRINT",FACE,{"disambiguationData":[TD([[makeQuery(id+"F0.imprint","IMPRINT",EDGE,{"disambiguationData":[TD([[subQ2,-1.0]])],"derivedFrom":subQ1}),-1.0]])]});}
            var Q59;
            {var subQ0=sQuery(id+"F0.wireOp",EDGE,"E8.12.3");var subQ1=sQuery(id+"F0.wireOp",EDGE,"E2");var subQ2=makeQuery(id+"F0.imprint","INTERSECT",VERTEX,{"derivedFrom":[subQ1,subQ0]});Q59=makeQuery(id+"F0.imprint","IMPRINT",FACE,{"disambiguationData":[TD([[makeQuery(id+"F0.imprint","IMPRINT",EDGE,{"disambiguationData":[TD([[subQ2,-1.0]])],"derivedFrom":subQ1}),-1.0]])]});}
            var Q60;
            {var subQ0=sQuery(id+"F0.wireOp",EDGE,"E8.13.3");var subQ1=sQuery(id+"F0.wireOp",EDGE,"E2");var subQ2=makeQuery(id+"F0.imprint","INTERSECT",VERTEX,{"derivedFrom":[subQ1,subQ0]});Q60=makeQuery(id+"F0.imprint","IMPRINT",FACE,{"disambiguationData":[TD([[makeQuery(id+"F0.imprint","IMPRINT",EDGE,{"disambiguationData":[TD([[subQ2,-1.0]])],"derivedFrom":subQ1}),-1.0]])]});}
            var Q61;
            {var subQ0=sQuery(id+"F0.wireOp",EDGE,"E8.14.3");var subQ1=sQuery(id+"F0.wireOp",EDGE,"E2");var subQ2=makeQuery(id+"F0.imprint","INTERSECT",VERTEX,{"derivedFrom":[subQ1,subQ0]});Q61=makeQuery(id+"F0.imprint","IMPRINT",FACE,{"disambiguationData":[TD([[makeQuery(id+"F0.imprint","IMPRINT",EDGE,{"disambiguationData":[TD([[subQ2,-1.0]])],"derivedFrom":subQ1}),-1.0]])]});}
            var Q62;
            {var subQ0=sQuery(id+"F0.wireOp",EDGE,"E8.15.3");var subQ1=sQuery(id+"F0.wireOp",EDGE,"E2");var subQ2=makeQuery(id+"F0.imprint","INTERSECT",VERTEX,{"derivedFrom":[subQ1,subQ0]});Q62=makeQuery(id+"F0.imprint","IMPRINT",FACE,{"disambiguationData":[TD([[makeQuery(id+"F0.imprint","IMPRINT",EDGE,{"disambiguationData":[TD([[subQ2,-1.0]])],"derivedFrom":subQ1}),-1.0]])]});}
            var Q63;
            {var subQ0=sQuery(id+"F0.wireOp",EDGE,"E8.16.3");var subQ1=sQuery(id+"F0.wireOp",EDGE,"E2");var subQ2=makeQuery(id+"F0.imprint","INTERSECT",VERTEX,{"derivedFrom":[subQ1,subQ0]});Q63=makeQuery(id+"F0.imprint","IMPRINT",FACE,{"disambiguationData":[TD([[makeQuery(id+"F0.imprint","IMPRINT",EDGE,{"disambiguationData":[TD([[subQ2,-1.0]])],"derivedFrom":subQ1}),-1.0]])]});}
            var Q64;
            {var subQ0=sQuery(id+"F0.wireOp",EDGE,"E8.17.3");var subQ1=sQuery(id+"F0.wireOp",EDGE,"E2");var subQ2=makeQuery(id+"F0.imprint","INTERSECT",VERTEX,{"derivedFrom":[subQ1,subQ0]});Q64=makeQuery(id+"F0.imprint","IMPRINT",FACE,{"disambiguationData":[TD([[makeQuery(id+"F0.imprint","IMPRINT",EDGE,{"disambiguationData":[TD([[subQ2,-1.0]])],"derivedFrom":subQ1}),-1.0]])]});}
            var Q65;
            {var subQ0=sQuery(id+"F0.wireOp",EDGE,"E8.18.3");var subQ1=sQuery(id+"F0.wireOp",EDGE,"E2");var subQ2=makeQuery(id+"F0.imprint","INTERSECT",VERTEX,{"derivedFrom":[subQ1,subQ0]});Q65=makeQuery(id+"F0.imprint","IMPRINT",FACE,{"disambiguationData":[TD([[makeQuery(id+"F0.imprint","IMPRINT",EDGE,{"disambiguationData":[TD([[subQ2,-1.0]])],"derivedFrom":subQ1}),-1.0]])]});}
            var Q66;
            {var subQ0=sQuery(id+"F0.wireOp",EDGE,"E8.19.3");var subQ1=sQuery(id+"F0.wireOp",EDGE,"E2");var subQ2=makeQuery(id+"F0.imprint","INTERSECT",VERTEX,{"derivedFrom":[subQ1,subQ0]});Q66=makeQuery(id+"F0.imprint","IMPRINT",FACE,{"disambiguationData":[TD([[makeQuery(id+"F0.imprint","IMPRINT",EDGE,{"disambiguationData":[TD([[subQ2,-1.0]])],"derivedFrom":subQ1}),-1.0]])]});}
            var Q67;
            {var subQ0=sQuery(id+"F0.wireOp",EDGE,"E8.20.3");var subQ1=sQuery(id+"F0.wireOp",EDGE,"E2");var subQ2=makeQuery(id+"F0.imprint","INTERSECT",VERTEX,{"derivedFrom":[subQ1,subQ0]});Q67=makeQuery(id+"F0.imprint","IMPRINT",FACE,{"disambiguationData":[TD([[makeQuery(id+"F0.imprint","IMPRINT",EDGE,{"disambiguationData":[TD([[subQ2,-1.0]])],"derivedFrom":subQ1}),-1.0]])]});}
            var Q68;
            {var subQ0=sQuery(id+"F0.wireOp",EDGE,"E8.21.3");var subQ1=sQuery(id+"F0.wireOp",EDGE,"E2");var subQ2=makeQuery(id+"F0.imprint","INTERSECT",VERTEX,{"derivedFrom":[subQ1,subQ0]});Q68=makeQuery(id+"F0.imprint","IMPRINT",FACE,{"disambiguationData":[TD([[makeQuery(id+"F0.imprint","IMPRINT",EDGE,{"disambiguationData":[TD([[subQ2,-1.0]])],"derivedFrom":subQ1}),-1.0]])]});}
            var Q69;
            {var subQ0=sQuery(id+"F0.wireOp",EDGE,"E8.22.3");var subQ1=sQuery(id+"F0.wireOp",EDGE,"E2");var subQ2=makeQuery(id+"F0.imprint","INTERSECT",VERTEX,{"derivedFrom":[subQ1,subQ0]});Q69=makeQuery(id+"F0.imprint","IMPRINT",FACE,{"disambiguationData":[TD([[makeQuery(id+"F0.imprint","IMPRINT",EDGE,{"disambiguationData":[TD([[subQ2,-1.0]])],"derivedFrom":subQ1}),-1.0]])]});}
            var Q70;
            {var subQ0=sQuery(id+"F0.wireOp",EDGE,"E8.23.3");var subQ1=sQuery(id+"F0.wireOp",EDGE,"E2");var subQ2=makeQuery(id+"F0.imprint","INTERSECT",VERTEX,{"derivedFrom":[subQ1,subQ0]});Q70=makeQuery(id+"F0.imprint","IMPRINT",FACE,{"disambiguationData":[TD([[makeQuery(id+"F0.imprint","IMPRINT",EDGE,{"disambiguationData":[TD([[subQ2,-1.0]])],"derivedFrom":subQ1}),-1.0]])]});}
            var Q71;
            {var subQ0=sQuery(id+"F0.wireOp",EDGE,"E4");var subQ1=sQuery(id+"F0.wireOp",EDGE,"E2");var subQ2=makeQuery(id+"F0.imprint","INTERSECT",VERTEX,{"derivedFrom":[subQ1,subQ0]});Q71=makeQuery(id+"F0.imprint","IMPRINT",FACE,{"disambiguationData":[TD([[makeQuery(id+"F0.imprint","IMPRINT",EDGE,{"disambiguationData":[TD([[subQ2,1.0]])],"derivedFrom":subQ1}),-1.0]])]});}
            var Q72;
            {var subQ0=sQuery(id+"F0.wireOp",EDGE,"E8.10.0");var subQ1=sQuery(id+"F0.wireOp",EDGE,"E1");var subQ2=makeQuery(id+"F0.imprint","INTERSECT",VERTEX,{"derivedFrom":[subQ1,subQ0]});Q72=makeQuery(id+"F0.imprint","IMPRINT",FACE,{"disambiguationData":[TD([[makeQuery(id+"F0.imprint","IMPRINT",EDGE,{"disambiguationData":[TD([[subQ2,1.0]])],"derivedFrom":subQ1}),-1.0]])]});}
            var Q73;
            Q73=makeQuery(id+"F0.imprint","IMPRINT",FACE,{"disambiguationData":[TD([[makeQuery(id+"F0.imprint","IMPRINT",EDGE,{"derivedFrom":sQuery(id+"F0.wireOp",EDGE,"E0")}),-1.0]])]});
            var Q74;
            {var subQ0=sQuery(id+"F0.wireOp",EDGE,"E8.9.0");var subQ1=sQuery(id+"F0.wireOp",EDGE,"E1");var subQ2=makeQuery(id+"F0.imprint","INTERSECT",VERTEX,{"derivedFrom":[subQ1,subQ0]});Q74=makeQuery(id+"F0.imprint","IMPRINT",FACE,{"disambiguationData":[TD([[makeQuery(id+"F0.imprint","IMPRINT",EDGE,{"disambiguationData":[TD([[subQ2,1.0]])],"derivedFrom":subQ1}),-1.0]])]});}
            var Q75;
            {var subQ0=sQuery(id+"F0.wireOp",EDGE,"E8.8.0");var subQ1=sQuery(id+"F0.wireOp",EDGE,"E1");var subQ2=makeQuery(id+"F0.imprint","INTERSECT",VERTEX,{"derivedFrom":[subQ1,subQ0]});Q75=makeQuery(id+"F0.imprint","IMPRINT",FACE,{"disambiguationData":[TD([[makeQuery(id+"F0.imprint","IMPRINT",EDGE,{"disambiguationData":[TD([[subQ2,1.0]])],"derivedFrom":subQ1}),-1.0]])]});}
            var Q76;
            {var subQ0=sQuery(id+"F0.wireOp",EDGE,"E8.7.0");var subQ1=sQuery(id+"F0.wireOp",EDGE,"E1");var subQ2=makeQuery(id+"F0.imprint","INTERSECT",VERTEX,{"derivedFrom":[subQ1,subQ0]});Q76=makeQuery(id+"F0.imprint","IMPRINT",FACE,{"disambiguationData":[TD([[makeQuery(id+"F0.imprint","IMPRINT",EDGE,{"disambiguationData":[TD([[subQ2,1.0]])],"derivedFrom":subQ1}),-1.0]])]});}
            var Q77;
            {var subQ0=sQuery(id+"F0.wireOp",EDGE,"E8.6.0");var subQ1=sQuery(id+"F0.wireOp",EDGE,"E1");var subQ2=makeQuery(id+"F0.imprint","INTERSECT",VERTEX,{"derivedFrom":[subQ1,subQ0]});Q77=makeQuery(id+"F0.imprint","IMPRINT",FACE,{"disambiguationData":[TD([[makeQuery(id+"F0.imprint","IMPRINT",EDGE,{"disambiguationData":[TD([[subQ2,1.0]])],"derivedFrom":subQ1}),-1.0]])]});}
            var Q78;
            {var subQ0=sQuery(id+"F0.wireOp",EDGE,"E8.5.0");var subQ1=sQuery(id+"F0.wireOp",EDGE,"E1");var subQ2=makeQuery(id+"F0.imprint","INTERSECT",VERTEX,{"derivedFrom":[subQ1,subQ0]});Q78=makeQuery(id+"F0.imprint","IMPRINT",FACE,{"disambiguationData":[TD([[makeQuery(id+"F0.imprint","IMPRINT",EDGE,{"disambiguationData":[TD([[subQ2,1.0]])],"derivedFrom":subQ1}),-1.0]])]});}
            var Q79;
            {var subQ0=sQuery(id+"F0.wireOp",EDGE,"E8.4.0");var subQ1=sQuery(id+"F0.wireOp",EDGE,"E1");var subQ2=makeQuery(id+"F0.imprint","INTERSECT",VERTEX,{"derivedFrom":[subQ1,subQ0]});Q79=makeQuery(id+"F0.imprint","IMPRINT",FACE,{"disambiguationData":[TD([[makeQuery(id+"F0.imprint","IMPRINT",EDGE,{"disambiguationData":[TD([[subQ2,1.0]])],"derivedFrom":subQ1}),-1.0]])]});}
            var Q80;
            {var subQ0=sQuery(id+"F0.wireOp",EDGE,"E8.3.0");var subQ1=sQuery(id+"F0.wireOp",EDGE,"E1");var subQ2=makeQuery(id+"F0.imprint","INTERSECT",VERTEX,{"derivedFrom":[subQ1,subQ0]});Q80=makeQuery(id+"F0.imprint","IMPRINT",FACE,{"disambiguationData":[TD([[makeQuery(id+"F0.imprint","IMPRINT",EDGE,{"disambiguationData":[TD([[subQ2,1.0]])],"derivedFrom":subQ1}),-1.0]])]});}
            var Q81;
            {var subQ0=sQuery(id+"F0.wireOp",EDGE,"E8.2.0");var subQ1=sQuery(id+"F0.wireOp",EDGE,"E1");var subQ2=makeQuery(id+"F0.imprint","INTERSECT",VERTEX,{"derivedFrom":[subQ1,subQ0]});Q81=makeQuery(id+"F0.imprint","IMPRINT",FACE,{"disambiguationData":[TD([[makeQuery(id+"F0.imprint","IMPRINT",EDGE,{"disambiguationData":[TD([[subQ2,1.0]])],"derivedFrom":subQ1}),-1.0]])]});}
            var Q82;
            {var subQ0=sQuery(id+"F0.wireOp",EDGE,"E8.1.0");var subQ1=sQuery(id+"F0.wireOp",EDGE,"E1");var subQ2=makeQuery(id+"F0.imprint","INTERSECT",VERTEX,{"derivedFrom":[subQ1,subQ0]});Q82=makeQuery(id+"F0.imprint","IMPRINT",FACE,{"disambiguationData":[TD([[makeQuery(id+"F0.imprint","IMPRINT",EDGE,{"disambiguationData":[TD([[subQ2,1.0]])],"derivedFrom":subQ1}),-1.0]])]});}
            var Q83;
            {var subQ0=sQuery(id+"F0.wireOp",EDGE,"E4");var subQ1=sQuery(id+"F0.wireOp",EDGE,"E1");var subQ2=makeQuery(id+"F0.imprint","INTERSECT",VERTEX,{"derivedFrom":[subQ1,subQ0]});Q83=makeQuery(id+"F0.imprint","IMPRINT",FACE,{"disambiguationData":[TD([[makeQuery(id+"F0.imprint","IMPRINT",EDGE,{"disambiguationData":[TD([[subQ2,1.0]])],"derivedFrom":subQ1}),-1.0]])]});}
            var Q84;
            {var subQ0=sQuery(id+"F0.wireOp",EDGE,"E8.23.0");var subQ1=sQuery(id+"F0.wireOp",EDGE,"E1");var subQ2=makeQuery(id+"F0.imprint","INTERSECT",VERTEX,{"derivedFrom":[subQ1,subQ0]});Q84=makeQuery(id+"F0.imprint","IMPRINT",FACE,{"disambiguationData":[TD([[makeQuery(id+"F0.imprint","IMPRINT",EDGE,{"disambiguationData":[TD([[subQ2,1.0]])],"derivedFrom":subQ1}),-1.0]])]});}
            var Q85;
            {var subQ0=sQuery(id+"F0.wireOp",EDGE,"E8.22.0");var subQ1=sQuery(id+"F0.wireOp",EDGE,"E1");var subQ2=makeQuery(id+"F0.imprint","INTERSECT",VERTEX,{"derivedFrom":[subQ1,subQ0]});Q85=makeQuery(id+"F0.imprint","IMPRINT",FACE,{"disambiguationData":[TD([[makeQuery(id+"F0.imprint","IMPRINT",EDGE,{"disambiguationData":[TD([[subQ2,1.0]])],"derivedFrom":subQ1}),-1.0]])]});}
            var Q86;
            {var subQ0=sQuery(id+"F0.wireOp",EDGE,"E8.21.0");var subQ1=sQuery(id+"F0.wireOp",EDGE,"E1");var subQ2=makeQuery(id+"F0.imprint","INTERSECT",VERTEX,{"derivedFrom":[subQ1,subQ0]});Q86=makeQuery(id+"F0.imprint","IMPRINT",FACE,{"disambiguationData":[TD([[makeQuery(id+"F0.imprint","IMPRINT",EDGE,{"disambiguationData":[TD([[subQ2,1.0]])],"derivedFrom":subQ1}),-1.0]])]});}
            var Q87;
            {var subQ0=sQuery(id+"F0.wireOp",EDGE,"E8.20.0");var subQ1=sQuery(id+"F0.wireOp",EDGE,"E1");var subQ2=makeQuery(id+"F0.imprint","INTERSECT",VERTEX,{"derivedFrom":[subQ1,subQ0]});Q87=makeQuery(id+"F0.imprint","IMPRINT",FACE,{"disambiguationData":[TD([[makeQuery(id+"F0.imprint","IMPRINT",EDGE,{"disambiguationData":[TD([[subQ2,1.0]])],"derivedFrom":subQ1}),-1.0]])]});}
            var Q88;
            {var subQ0=sQuery(id+"F0.wireOp",EDGE,"E8.19.0");var subQ1=sQuery(id+"F0.wireOp",EDGE,"E1");var subQ2=makeQuery(id+"F0.imprint","INTERSECT",VERTEX,{"derivedFrom":[subQ1,subQ0]});Q88=makeQuery(id+"F0.imprint","IMPRINT",FACE,{"disambiguationData":[TD([[makeQuery(id+"F0.imprint","IMPRINT",EDGE,{"disambiguationData":[TD([[subQ2,1.0]])],"derivedFrom":subQ1}),-1.0]])]});}
            var Q89;
            {var subQ0=sQuery(id+"F0.wireOp",EDGE,"E8.18.0");var subQ1=sQuery(id+"F0.wireOp",EDGE,"E1");var subQ2=makeQuery(id+"F0.imprint","INTERSECT",VERTEX,{"derivedFrom":[subQ1,subQ0]});Q89=makeQuery(id+"F0.imprint","IMPRINT",FACE,{"disambiguationData":[TD([[makeQuery(id+"F0.imprint","IMPRINT",EDGE,{"disambiguationData":[TD([[subQ2,1.0]])],"derivedFrom":subQ1}),-1.0]])]});}
            var Q90;
            {var subQ0=sQuery(id+"F0.wireOp",EDGE,"E8.17.0");var subQ1=sQuery(id+"F0.wireOp",EDGE,"E1");var subQ2=makeQuery(id+"F0.imprint","INTERSECT",VERTEX,{"derivedFrom":[subQ1,subQ0]});Q90=makeQuery(id+"F0.imprint","IMPRINT",FACE,{"disambiguationData":[TD([[makeQuery(id+"F0.imprint","IMPRINT",EDGE,{"disambiguationData":[TD([[subQ2,1.0]])],"derivedFrom":subQ1}),-1.0]])]});}
            var Q91;
            {var subQ0=sQuery(id+"F0.wireOp",EDGE,"E8.16.0");var subQ1=sQuery(id+"F0.wireOp",EDGE,"E1");var subQ2=makeQuery(id+"F0.imprint","INTERSECT",VERTEX,{"derivedFrom":[subQ1,subQ0]});Q91=makeQuery(id+"F0.imprint","IMPRINT",FACE,{"disambiguationData":[TD([[makeQuery(id+"F0.imprint","IMPRINT",EDGE,{"disambiguationData":[TD([[subQ2,1.0]])],"derivedFrom":subQ1}),-1.0]])]});}
            var Q92;
            {var subQ0=sQuery(id+"F0.wireOp",EDGE,"E8.15.0");var subQ1=sQuery(id+"F0.wireOp",EDGE,"E1");var subQ2=makeQuery(id+"F0.imprint","INTERSECT",VERTEX,{"derivedFrom":[subQ1,subQ0]});Q92=makeQuery(id+"F0.imprint","IMPRINT",FACE,{"disambiguationData":[TD([[makeQuery(id+"F0.imprint","IMPRINT",EDGE,{"disambiguationData":[TD([[subQ2,1.0]])],"derivedFrom":subQ1}),-1.0]])]});}
            var Q93;
            {var subQ0=sQuery(id+"F0.wireOp",EDGE,"E8.14.0");var subQ1=sQuery(id+"F0.wireOp",EDGE,"E1");var subQ2=makeQuery(id+"F0.imprint","INTERSECT",VERTEX,{"derivedFrom":[subQ1,subQ0]});Q93=makeQuery(id+"F0.imprint","IMPRINT",FACE,{"disambiguationData":[TD([[makeQuery(id+"F0.imprint","IMPRINT",EDGE,{"disambiguationData":[TD([[subQ2,1.0]])],"derivedFrom":subQ1}),-1.0]])]});}
            var Q94;
            {var subQ0=sQuery(id+"F0.wireOp",EDGE,"E8.13.0");var subQ1=sQuery(id+"F0.wireOp",EDGE,"E1");var subQ2=makeQuery(id+"F0.imprint","INTERSECT",VERTEX,{"derivedFrom":[subQ1,subQ0]});Q94=makeQuery(id+"F0.imprint","IMPRINT",FACE,{"disambiguationData":[TD([[makeQuery(id+"F0.imprint","IMPRINT",EDGE,{"disambiguationData":[TD([[subQ2,1.0]])],"derivedFrom":subQ1}),-1.0]])]});}
            var Q95;
            {var subQ0=sQuery(id+"F0.wireOp",EDGE,"E8.12.0");var subQ1=sQuery(id+"F0.wireOp",EDGE,"E1");var subQ2=makeQuery(id+"F0.imprint","INTERSECT",VERTEX,{"derivedFrom":[subQ1,subQ0]});Q95=makeQuery(id+"F0.imprint","IMPRINT",FACE,{"disambiguationData":[TD([[makeQuery(id+"F0.imprint","IMPRINT",EDGE,{"disambiguationData":[TD([[subQ2,1.0]])],"derivedFrom":subQ1}),-1.0]])]});}
            var Q96;
            {var subQ0=sQuery(id+"F0.wireOp",EDGE,"E8.11.0");var subQ1=sQuery(id+"F0.wireOp",EDGE,"E1");var subQ2=makeQuery(id+"F0.imprint","INTERSECT",VERTEX,{"derivedFrom":[subQ1,subQ0]});Q96=makeQuery(id+"F0.imprint","IMPRINT",FACE,{"disambiguationData":[TD([[makeQuery(id+"F0.imprint","IMPRINT",EDGE,{"disambiguationData":[TD([[subQ2,1.0]])],"derivedFrom":subQ1}),-1.0]])]});}
            extrude(context, id + "F1", {"entities" : qUnion([Q0, Q1, Q2, Q3, Q4, Q5, Q6, Q7, Q8, Q9, Q10, Q11, Q12, Q13, Q14, Q15, Q16, Q17, Q18, Q19, Q20, Q21, Q22, Q23, Q24, Q25, Q26, Q27, Q28, Q29, Q30, Q31, Q32, Q33, Q34, Q35, Q36, Q37, Q38, Q39, Q40, Q41, Q42, Q43, Q44, Q45, Q46, Q47, Q48, Q49, Q50, Q51, Q52, Q53, Q54, Q55, Q56, Q57, Q58, Q59, Q60, Q61, Q62, Q63, Q64, Q65, Q66, Q67, Q68, Q69, Q70, Q71, Q72, Q73, Q74, Q75, Q76, Q77, Q78, Q79, Q80, Q81, Q82, Q83, Q84, Q85, Q86, Q87, Q88, Q89, Q90, Q91, Q92, Q93, Q94, Q95, Q96]), "depth" : 10 * mm, "offsetDistance" : 25 * mm});
        }
        {
            var Q0;
            Q0=makeQuery(id+"F1.opExtrude","CAP_EDGE",EDGE,{"disambiguationData":[OSD([sQuery(id+"F0.wireOp",EDGE,"E8.16.1"),sQuery(id+"F0.wireOp",EDGE,"E8.16.2")])],"isStart":false});
            var Q1;
            Q1=makeQuery(id+"F1.opExtrude","CAP_EDGE",EDGE,{"disambiguationData":[OSD([sQuery(id+"F0.wireOp",EDGE,"E8.17.1"),sQuery(id+"F0.wireOp",EDGE,"E8.17.2")])],"isStart":false});
            var Q2;
            Q2=makeQuery(id+"F1.opExtrude","CAP_EDGE",EDGE,{"disambiguationData":[OSD([sQuery(id+"F0.wireOp",EDGE,"E8.18.1"),sQuery(id+"F0.wireOp",EDGE,"E8.18.2")])],"isStart":false});
            var Q3;
            Q3=makeQuery(id+"F1.opExtrude","CAP_EDGE",EDGE,{"disambiguationData":[OSD([sQuery(id+"F0.wireOp",EDGE,"E8.19.1"),sQuery(id+"F0.wireOp",EDGE,"E8.19.2")])],"isStart":false});
            var Q4;
            Q4=makeQuery(id+"F1.opExtrude","CAP_EDGE",EDGE,{"disambiguationData":[OSD([sQuery(id+"F0.wireOp",EDGE,"E8.20.1"),sQuery(id+"F0.wireOp",EDGE,"E8.20.2")])],"isStart":false});
            var Q5;
            Q5=makeQuery(id+"F1.opExtrude","CAP_EDGE",EDGE,{"disambiguationData":[OSD([sQuery(id+"F0.wireOp",EDGE,"E8.21.1"),sQuery(id+"F0.wireOp",EDGE,"E8.21.2")])],"isStart":false});
            var Q6;
            Q6=makeQuery(id+"F1.opExtrude","CAP_EDGE",EDGE,{"disambiguationData":[OSD([sQuery(id+"F0.wireOp",EDGE,"E8.22.1"),sQuery(id+"F0.wireOp",EDGE,"E8.22.2")])],"isStart":false});
            var Q7;
            Q7=makeQuery(id+"F1.opExtrude","CAP_EDGE",EDGE,{"disambiguationData":[OSD([sQuery(id+"F0.wireOp",EDGE,"E8.15.1"),sQuery(id+"F0.wireOp",EDGE,"E8.15.2")])],"isStart":false});
            var Q8;
            Q8=makeQuery(id+"F1.opExtrude","CAP_EDGE",EDGE,{"disambiguationData":[OSD([sQuery(id+"F0.wireOp",EDGE,"E8.14.1"),sQuery(id+"F0.wireOp",EDGE,"E8.14.2")])],"isStart":false});
            var Q9;
            Q9=makeQuery(id+"F1.opExtrude","CAP_EDGE",EDGE,{"disambiguationData":[OSD([sQuery(id+"F0.wireOp",EDGE,"E8.13.1"),sQuery(id+"F0.wireOp",EDGE,"E8.13.2")])],"isStart":false});
            var Q10;
            Q10=makeQuery(id+"F1.opExtrude","CAP_EDGE",EDGE,{"disambiguationData":[OSD([sQuery(id+"F0.wireOp",EDGE,"E8.12.1"),sQuery(id+"F0.wireOp",EDGE,"E8.12.2")])],"isStart":false});
            var Q11;
            Q11=makeQuery(id+"F1.opExtrude","CAP_EDGE",EDGE,{"disambiguationData":[OSD([sQuery(id+"F0.wireOp",EDGE,"E8.11.1"),sQuery(id+"F0.wireOp",EDGE,"E8.11.2")])],"isStart":false});
            var Q12;
            Q12=makeQuery(id+"F1.opExtrude","CAP_EDGE",EDGE,{"disambiguationData":[OSD([sQuery(id+"F0.wireOp",EDGE,"E8.10.1"),sQuery(id+"F0.wireOp",EDGE,"E8.10.2")])],"isStart":false});
            var Q13;
            Q13=makeQuery(id+"F1.opExtrude","CAP_EDGE",EDGE,{"disambiguationData":[OSD([sQuery(id+"F0.wireOp",EDGE,"E8.9.1"),sQuery(id+"F0.wireOp",EDGE,"E8.9.2")])],"isStart":false});
            var Q14;
            Q14=makeQuery(id+"F1.opExtrude","CAP_EDGE",EDGE,{"disambiguationData":[OSD([sQuery(id+"F0.wireOp",EDGE,"E8.8.1"),sQuery(id+"F0.wireOp",EDGE,"E8.8.2")])],"isStart":false});
            var Q15;
            Q15=makeQuery(id+"F1.opExtrude","CAP_EDGE",EDGE,{"disambiguationData":[OSD([sQuery(id+"F0.wireOp",EDGE,"E8.7.1"),sQuery(id+"F0.wireOp",EDGE,"E8.7.2")])],"isStart":false});
            var Q16;
            Q16=makeQuery(id+"F1.opExtrude","CAP_EDGE",EDGE,{"disambiguationData":[OSD([sQuery(id+"F0.wireOp",EDGE,"E8.6.1"),sQuery(id+"F0.wireOp",EDGE,"E8.6.2")])],"isStart":false});
            var Q17;
            Q17=makeQuery(id+"F1.opExtrude","CAP_EDGE",EDGE,{"disambiguationData":[OSD([sQuery(id+"F0.wireOp",EDGE,"E8.5.1"),sQuery(id+"F0.wireOp",EDGE,"E8.5.2")])],"isStart":false});
            var Q18;
            Q18=makeQuery(id+"F1.opExtrude","CAP_EDGE",EDGE,{"disambiguationData":[OSD([sQuery(id+"F0.wireOp",EDGE,"E8.4.1"),sQuery(id+"F0.wireOp",EDGE,"E8.4.2")])],"isStart":false});
            var Q19;
            Q19=makeQuery(id+"F1.opExtrude","CAP_EDGE",EDGE,{"disambiguationData":[OSD([sQuery(id+"F0.wireOp",EDGE,"E8.3.1"),sQuery(id+"F0.wireOp",EDGE,"E8.3.2")])],"isStart":false});
            var Q20;
            Q20=makeQuery(id+"F1.opExtrude","CAP_EDGE",EDGE,{"disambiguationData":[OSD([sQuery(id+"F0.wireOp",EDGE,"E8.2.1"),sQuery(id+"F0.wireOp",EDGE,"E8.2.2")])],"isStart":false});
            var Q21;
            Q21=makeQuery(id+"F1.opExtrude","CAP_EDGE",EDGE,{"disambiguationData":[OSD([sQuery(id+"F0.wireOp",EDGE,"E8.23.1"),sQuery(id+"F0.wireOp",EDGE,"E8.23.2")])],"isStart":false});
            var Q22;
            Q22=makeQuery(id+"F1.opExtrude","CAP_EDGE",EDGE,{"disambiguationData":[OSD([sQuery(id+"F0.wireOp",EDGE,"E5"),sQuery(id+"F0.wireOp",EDGE,"E7.MirrorCS")])],"isStart":false});
            var Q23;
            Q23=makeQuery(id+"F1.opExtrude","CAP_EDGE",EDGE,{"disambiguationData":[OSD([sQuery(id+"F0.wireOp",EDGE,"E8.1.1"),sQuery(id+"F0.wireOp",EDGE,"E8.1.2")])],"isStart":false});
            chamfer(context, id + "F2", {"entities" : qUnion([Q0, Q1, Q2, Q3, Q4, Q5, Q6, Q7, Q8, Q9, Q10, Q11, Q12, Q13, Q14, Q15, Q16, Q17, Q18, Q19, Q20, Q21, Q22, Q23]), "chamferType" : ChamferType.TWO_OFFSETS, "width1" : 1.2 * mm, "oppositeDirection" : false, "width2" : 5 * mm, "tangentPropagation" : true});
        }
    });
